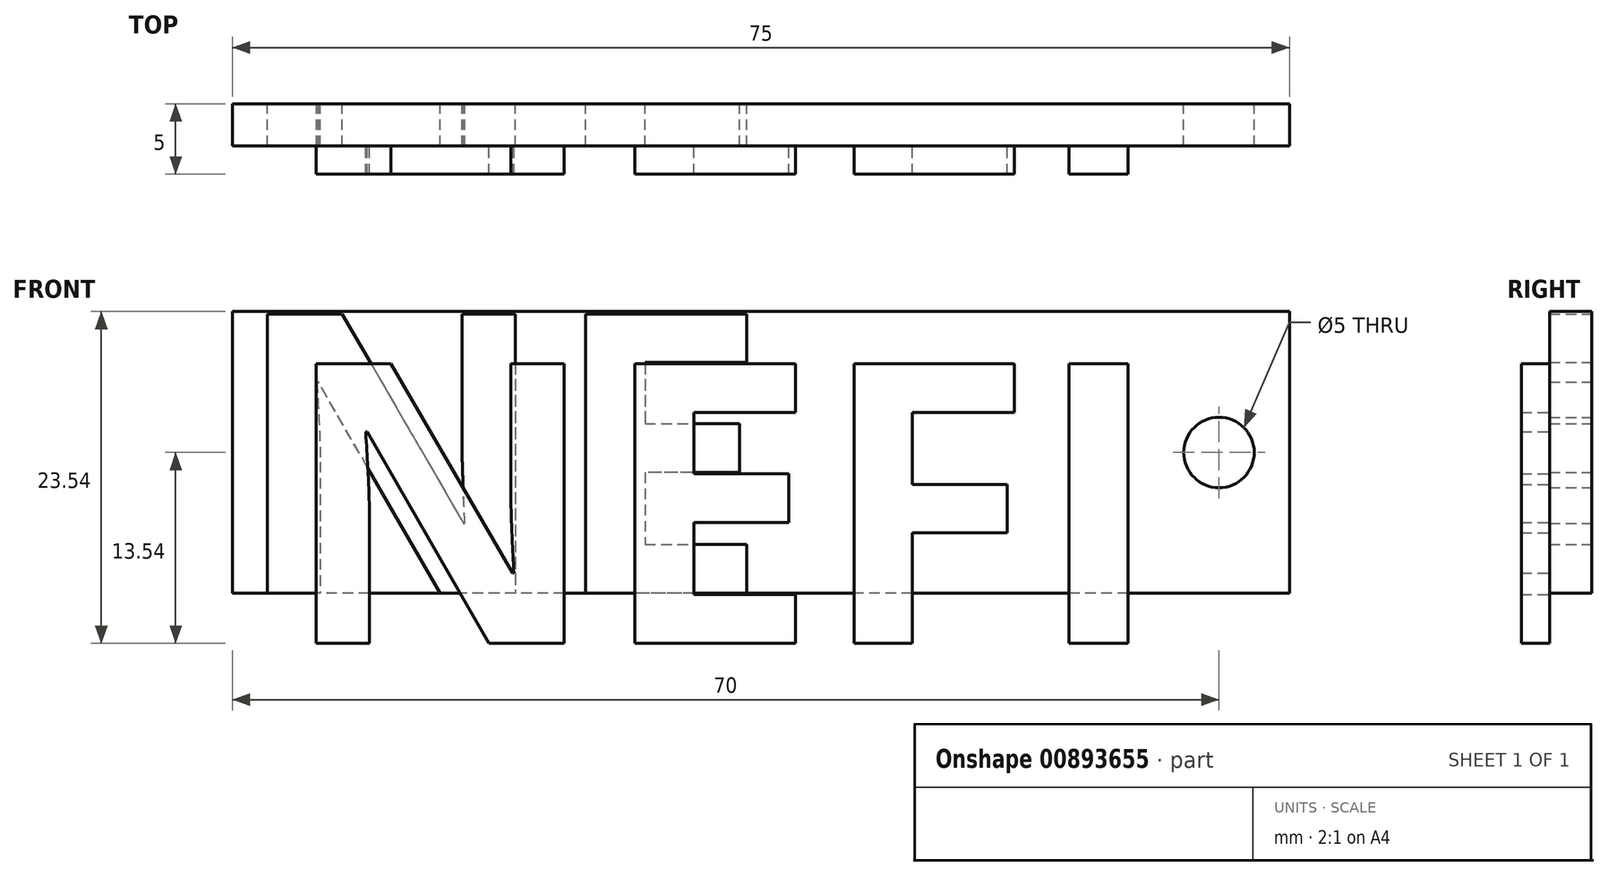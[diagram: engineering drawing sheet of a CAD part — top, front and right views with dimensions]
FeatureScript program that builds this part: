
annotation { "Feature Type Name" : "Feature", "Feature Type Description" : "" }
export const myFeature = defineFeature(function(context is Context, id is Id, definition is map)
    precondition{}
    {
        {
            var Q0;
            Q0=qCreatedBy(makeId("Front.planeOp"),FACE);
            var sketch = newSketch(context, id + "F0", { "sketchPlane" : qUnion([Q0])});
            skCircle(sketch, "E0", {"center": v(70, 14.29) * mm, "radius": 2.5 * mm});
            skLineSegment(sketch, "E1.bottom", {"start": v(75, 24.29) * mm, "end": v(0, 24.29) * mm});
            skLineSegment(sketch, "E1.top", {"start": v(75, 4.29) * mm, "end": v(0, 4.29) * mm});
            skLineSegment(sketch, "E1.left", {"start": v(75, 24.29) * mm, "end": v(75, 4.29) * mm});
            skLineSegment(sketch, "E1.right", {"start": v(0, 24.29) * mm, "end": v(0, 4.29) * mm});
            skText(sketch, "E2", { "text": "NEFI", "fontName": "OpenSans-Bold.ttf"});
            const initialGuessF0  = {"E2": [0, 0.00429, 1, 0, 0.02]};
            skSetInitialGuess(sketch, initialGuessF0);
            skSolve(sketch);
        }
        {
            var Q0;
            Q0=makeQuery(id+"F0.imprint","IMPRINT",FACE,{"disambiguationData":[TD([[makeQuery(id+"F0.imprint","IMPRINT",EDGE,{"derivedFrom":sQuery(id+"F0.wireOp",EDGE,"E1.bottom")}),1.0]])]});
            var Q1;
            {var subQ0=sQuery(id+"F0.wireOp",EDGE,"E2.sketch_text.stroke-37");Q1=makeQuery(id+"F0.imprint","IMPRINT",FACE,{"disambiguationData":[TD([[makeQuery(id+"F0.imprint","IMPRINT",EDGE,{"derivedFrom":subQ0}),-1.0]])]});}
            var Q2;
            Q2=makeQuery(id+"F0.imprint","IMPRINT",FACE,{"disambiguationData":[TD([[makeQuery(id+"F0.imprint","IMPRINT",EDGE,{"derivedFrom":sQuery(id+"F0.wireOp",EDGE,"E2.sketch_text.stroke-26")}),-1.0]])]});
            var Q3;
            Q3 = qSketchRegion(id + "F0", true);
            extrude(context, id + "F1", {"entities" : qUnion([Q0, Q1, Q2, Q3]), "depth" : 3 * mm, "offsetDistance" : 25 * mm});
        }
        {
            var Q0;
            Q0=makeQuery(id+"F1.opExtrude","CAP_FACE",FACE,{"disambiguationData":[OSD([sQuery(id+"F0.wireOp",EDGE,"E0"),sQuery(id+"F0.wireOp",EDGE,"E1.bottom"),sQuery(id+"F0.wireOp",EDGE,"E1.top"),sQuery(id+"F0.wireOp",EDGE,"E1.left"),sQuery(id+"F0.wireOp",EDGE,"E1.right"),sQuery(id+"F0.wireOp",EDGE,"E2.sketch_text.stroke-0"),sQuery(id+"F0.wireOp",EDGE,"E2.sketch_text.stroke-5"),sQuery(id+"F0.wireOp",EDGE,"E2.sketch_text.stroke-14"),sQuery(id+"F0.wireOp",EDGE,"E2.sketch_text.stroke-26"),sQuery(id+"F0.wireOp",EDGE,"E2.sketch_text.stroke-39")])],"isStart":false});
            var sketch = newSketch(context, id + "F2", { "sketchPlane" : qUnion([Q0])});
            skText(sketch, "E3", { "text": "NEFI", "fontName": "OpenSans-Bold.ttf"});
            const initialGuessF2  = {"E3": [0.00347, 0.00075, 1, 0, 0.02]};
            skSetInitialGuess(sketch, initialGuessF2);
            skSolve(sketch);
        }
        {
            var Q0;
            Q0=makeQuery(id+"F2.imprint","IMPRINT",FACE,{"disambiguationData":[TD([[makeQuery(id+"F2.imprint","IMPRINT",EDGE,{"derivedFrom":sQuery(id+"F2.wireOp",EDGE,"E3.sketch_text.stroke-26")}),-1.0]])]});
            var Q1;
            Q1=makeQuery(id+"F2.imprint","IMPRINT",FACE,{"disambiguationData":[TD([[makeQuery(id+"F2.imprint","IMPRINT",EDGE,{"derivedFrom":sQuery(id+"F2.wireOp",EDGE,"E3.sketch_text.stroke-14")}),-1.0]])]});
            var Q2;
            Q2=makeQuery(id+"F2.imprint","IMPRINT",FACE,{"disambiguationData":[TD([[makeQuery(id+"F2.imprint","IMPRINT",EDGE,{"derivedFrom":sQuery(id+"F2.wireOp",EDGE,"E3.sketch_text.stroke-36")}),-1.0]])]});
            var Q3;
            Q3 = qSketchRegion(id + "F2", true);
            extrude(context, id + "F3", {"entities" : qUnion([Q0, Q1, Q2, Q3]), "operationType" : NewBodyOperationType.ADD, "depth" : 2 * mm, "offsetDistance" : 25 * mm});
        }
    });
